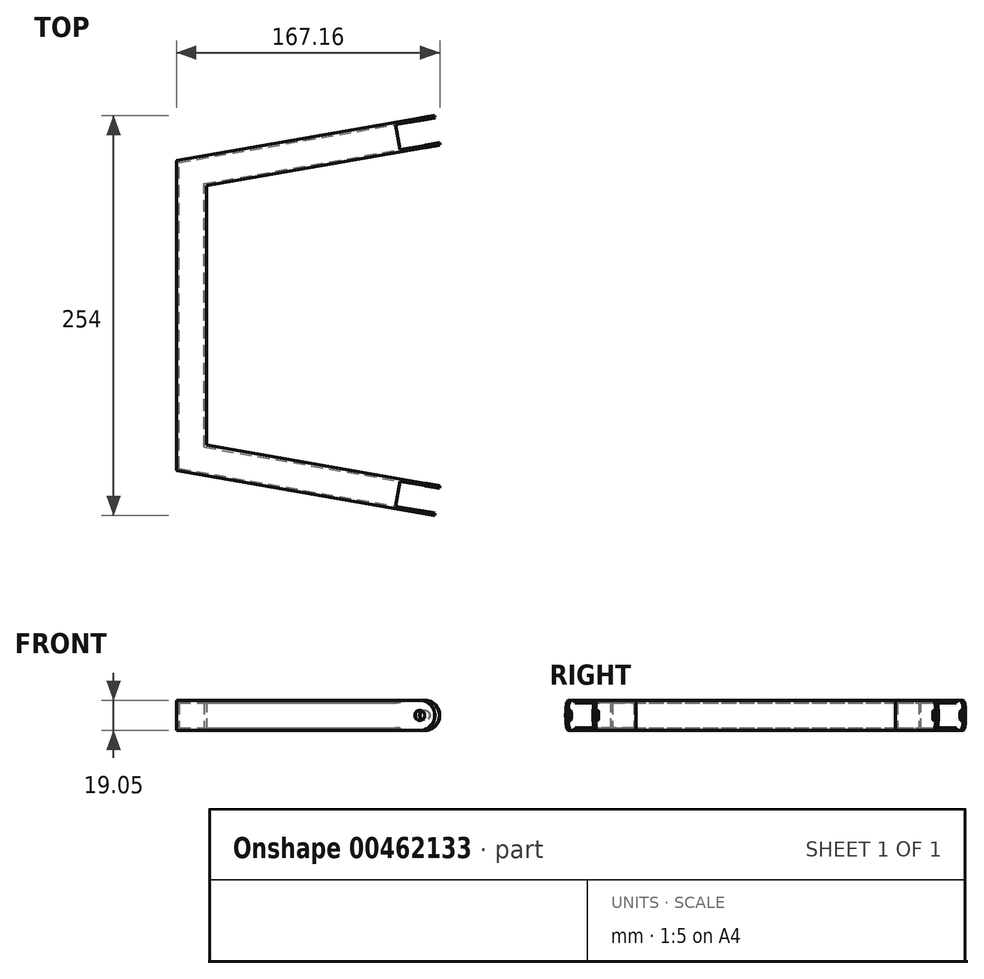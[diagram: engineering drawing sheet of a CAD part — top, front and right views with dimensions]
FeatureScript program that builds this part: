
annotation { "Feature Type Name" : "Feature", "Feature Type Description" : "" }
export const myFeature = defineFeature(function(context is Context, id is Id, definition is map)
    precondition{}
    {
        {
            var Q0;
            Q0=qCreatedBy(makeId("Top.planeOp"),FACE);
            var sketch = newSketch(context, id + "F0", { "sketchPlane" : qUnion([Q0])});
            skLineSegment(sketch, "E0.left", {"start": v(0, 28.57) * mm, "end": v(0, 225.43) * mm});
            skLineSegment(sketch, "E1", {"start": v(0, 127) * mm, "end": v(424.29, 127) * mm, "construction": true});
            skPoint(sketch, "E1.endSnap0", {"position": v(0, 127) * mm});
            skPoint(sketch, "E0.top.start.orphan", {"position": v(0, 254) * mm});
            skPoint(sketch, "E2.orphan", {"position": v(0, 0) * mm});
            skLineSegment(sketch, "E3", {"start": v(0, 225.43) * mm, "end": v(163.89, 254) * mm});
            skLineSegment(sketch, "E4", {"start": v(0, 28.57) * mm, "end": v(163.89, 0) * mm});
            skLineSegment(sketch, "E5.0", {"start": v(19.05, 209.4) * mm, "end": v(167.16, 235.23) * mm});
            skLineSegment(sketch, "E5.1", {"start": v(19.05, 44.6) * mm, "end": v(19.05, 209.4) * mm});
            skLineSegment(sketch, "E5.2", {"start": v(19.05, 44.6) * mm, "end": v(167.16, 18.77) * mm});
            skLineSegment(sketch, "E6", {"start": v(163.89, 254) * mm, "end": v(167.16, 235.23) * mm});
            skLineSegment(sketch, "E7", {"start": v(167.16, 18.77) * mm, "end": v(163.89, 0) * mm});
            skSolve(sketch);
        }
        {
            var Q0;
            Q0 = qSketchRegion(id + "F0", true);
            extrude(context, id + "F1", {"entities" : qUnion([Q0]), "depth" : 19.05 * mm});
        }
        {
            var Q0;
            Q0=makeQuery(id+"F1.opExtrude","SWEPT_FACE",FACE,{"disambiguationData":[OSD([sQuery(id+"F0.wireOp",EDGE,"E7")])]});
            var Q1;
            Q1=makeQuery(id+"F1.opExtrude","SWEPT_FACE",FACE,{"disambiguationData":[OSD([sQuery(id+"F0.wireOp",EDGE,"E6")])]});
            shell(context, id + "F2", {"entities" : qUnion([Q0, Q1]), "thickness" : 1.47 * mm});
        }
        {
            var Q0;
            Q0=makeQuery(id+"F1.opExtrude","SWEPT_FACE",FACE,{"disambiguationData":[OSD([sQuery(id+"F0.wireOp",EDGE,"E7")])]});
            var sketch = newSketch(context, id + "F3", { "sketchPlane" : qUnion([Q0])});
            skLineSegment(sketch, "E8.0", {"start": v(45.73, 19.05) * mm, "end": v(45.73, 0) * mm});
            skLineSegment(sketch, "E8.1", {"start": v(29.62, 19.05) * mm, "end": v(29.62, 0) * mm});
            skLineSegment(sketch, "E9.0", {"start": v(45.73, 19.05) * mm, "end": v(29.62, 19.05) * mm});
            skLineSegment(sketch, "E9.1", {"start": v(45.73, 0) * mm, "end": v(29.62, 0) * mm});
            skPoint(sketch, "E10.orphan", {"position": v(29.62, 17.58) * mm});
            skPoint(sketch, "E11.orphan", {"position": v(45.73, 17.58) * mm});
            skPoint(sketch, "E12.orphan", {"position": v(29.62, 1.47) * mm});
            skPoint(sketch, "E13.orphan", {"position": v(45.73, 1.47) * mm});
            skPoint(sketch, "E14.orphan", {"position": v(47.2, 0) * mm});
            skPoint(sketch, "E15.orphan", {"position": v(28.15, 0) * mm});
            skPoint(sketch, "E16.orphan", {"position": v(28.15, 19.05) * mm});
            skPoint(sketch, "E17.orphan", {"position": v(47.2, 19.05) * mm});
            skSolve(sketch);
        }
        {
            var Q0;
            Q0 = qSketchRegion(id + "F3", true);
            extrude(context, id + "F4", {"entities" : qUnion([Q0]), "operationType" : NewBodyOperationType.REMOVE, "oppositeDirection" : true, "depth" : 25.4 * mm});
        }
        {
            var Q0;
            {var subQ0=sQuery(id+"F0.wireOp",EDGE,"E4");var subQ1=sQuery(id+"F0.wireOp",EDGE,"E7");Q0=makeQuery(id+"F4.boolean.opBoolean","SPLIT",EDGE,{"disambiguationData":[TD([makeQuery(id+"F1.opExtrude","SWEPT_FACE",FACE,{"disambiguationData":[OSD([subQ0])]})])],"derivedFrom":makeQuery(id+"F1.opExtrude","CAP_EDGE",EDGE,{"disambiguationData":[OSD([subQ1])],"isStart":false})});}
            var Q1;
            {var subQ0=sQuery(id+"F0.wireOp",EDGE,"E5.2");var subQ1=sQuery(id+"F0.wireOp",EDGE,"E7");Q1=makeQuery(id+"F4.boolean.opBoolean","SPLIT",EDGE,{"disambiguationData":[TD([makeQuery(id+"F1.opExtrude","SWEPT_FACE",FACE,{"disambiguationData":[OSD([subQ0])]})])],"derivedFrom":makeQuery(id+"F1.opExtrude","CAP_EDGE",EDGE,{"disambiguationData":[OSD([subQ1])],"isStart":false})});}
            var Q2;
            {var subQ0=sQuery(id+"F0.wireOp",EDGE,"E4");var subQ1=sQuery(id+"F0.wireOp",EDGE,"E7");Q2=makeQuery(id+"F4.boolean.opBoolean","SPLIT",EDGE,{"disambiguationData":[TD([makeQuery(id+"F1.opExtrude","SWEPT_FACE",FACE,{"disambiguationData":[OSD([subQ0])]})])],"derivedFrom":makeQuery(id+"F1.opExtrude","CAP_EDGE",EDGE,{"disambiguationData":[OSD([subQ1])],"isStart":true})});}
            var Q3;
            {var subQ0=sQuery(id+"F0.wireOp",EDGE,"E5.2");var subQ1=sQuery(id+"F0.wireOp",EDGE,"E7");Q3=makeQuery(id+"F4.boolean.opBoolean","SPLIT",EDGE,{"disambiguationData":[TD([makeQuery(id+"F1.opExtrude","SWEPT_FACE",FACE,{"disambiguationData":[OSD([subQ0])]})])],"derivedFrom":makeQuery(id+"F1.opExtrude","CAP_EDGE",EDGE,{"disambiguationData":[OSD([subQ1])],"isStart":true})});}
            fillet(context, id + "F5", {"entities" : qUnion([Q0, Q1, Q2, Q3]), "radius" : 9.52 * mm, "tangentPropagation" : true, "allowEdgeOverflow" : false});
        }
        {
            var Q0;
            Q0=makeQuery(id+"F1.opExtrude","SWEPT_FACE",FACE,{"disambiguationData":[OSD([sQuery(id+"F0.wireOp",EDGE,"E4")])]});
            var sketch = newSketch(context, id + "F6", { "sketchPlane" : qUnion([Q0])});
            skCircle(sketch, "E18", {"center": v(151.93, 9.53) * mm, "radius": 3.18 * mm});
            skSolve(sketch);
        }
        {
            var Q0;
            Q0 = qSketchRegion(id + "F6", true);
            extrude(context, id + "F7", {"entities" : qUnion([Q0]), "operationType" : NewBodyOperationType.REMOVE, "endBound" : BoundingType.THROUGH_ALL, "oppositeDirection" : true, "depth" : 25.4 * mm});
        }
        {
            var Q0;
            Q0=makeQuery(id+"F1.opExtrude","SWEPT_FACE",FACE,{"disambiguationData":[OSD([sQuery(id+"F0.wireOp",EDGE,"E6")])]});
            var sketch = newSketch(context, id + "F8", { "sketchPlane" : qUnion([Q0])});
            skLineSegment(sketch, "E19.0", {"start": v(204.5, 19.05) * mm, "end": v(204.5, 0) * mm});
            skLineSegment(sketch, "E20.0", {"start": v(220.6, 19.05) * mm, "end": v(220.6, 0) * mm});
            skLineSegment(sketch, "E21.0", {"start": v(220.6, 0) * mm, "end": v(204.5, 0) * mm});
            skLineSegment(sketch, "E22.0", {"start": v(220.6, 19.05) * mm, "end": v(204.5, 19.05) * mm});
            skPoint(sketch, "E23.orphan", {"position": v(220.6, 1.47) * mm});
            skPoint(sketch, "E24.orphan", {"position": v(204.5, 1.47) * mm});
            skPoint(sketch, "E25.orphan", {"position": v(204.5, 17.58) * mm});
            skPoint(sketch, "E26.orphan", {"position": v(220.6, 17.58) * mm});
            skPoint(sketch, "E27.orphan", {"position": v(203.02, 0) * mm});
            skPoint(sketch, "E28.orphan", {"position": v(222.07, 0) * mm});
            skPoint(sketch, "E29.orphan", {"position": v(222.07, 19.05) * mm});
            skPoint(sketch, "E30.orphan", {"position": v(203.02, 19.05) * mm});
            skSolve(sketch);
        }
        {
            var Q0;
            Q0 = qSketchRegion(id + "F8", true);
            extrude(context, id + "F9", {"entities" : qUnion([Q0]), "operationType" : NewBodyOperationType.REMOVE, "oppositeDirection" : true, "depth" : 25.4 * mm});
        }
        {
            var Q0;
            {var subQ0=sQuery(id+"F0.wireOp",EDGE,"E3");var subQ1=sQuery(id+"F0.wireOp",EDGE,"E6");Q0=makeQuery(id+"F9.boolean.opBoolean","SPLIT",EDGE,{"disambiguationData":[TD([makeQuery(id+"F1.opExtrude","SWEPT_FACE",FACE,{"disambiguationData":[OSD([subQ0])]})])],"derivedFrom":makeQuery(id+"F1.opExtrude","CAP_EDGE",EDGE,{"disambiguationData":[OSD([subQ1])],"isStart":true})});}
            var Q1;
            {var subQ0=sQuery(id+"F0.wireOp",EDGE,"E3");var subQ1=sQuery(id+"F0.wireOp",EDGE,"E6");Q1=makeQuery(id+"F9.boolean.opBoolean","SPLIT",EDGE,{"disambiguationData":[TD([makeQuery(id+"F1.opExtrude","SWEPT_FACE",FACE,{"disambiguationData":[OSD([subQ0])]})])],"derivedFrom":makeQuery(id+"F1.opExtrude","CAP_EDGE",EDGE,{"disambiguationData":[OSD([subQ1])],"isStart":false})});}
            var Q2;
            {var subQ0=sQuery(id+"F0.wireOp",EDGE,"E5.0");var subQ1=sQuery(id+"F0.wireOp",EDGE,"E6");Q2=makeQuery(id+"F9.boolean.opBoolean","SPLIT",EDGE,{"disambiguationData":[TD([makeQuery(id+"F1.opExtrude","SWEPT_FACE",FACE,{"disambiguationData":[OSD([subQ0])]})])],"derivedFrom":makeQuery(id+"F1.opExtrude","CAP_EDGE",EDGE,{"disambiguationData":[OSD([subQ1])],"isStart":false})});}
            var Q3;
            {var subQ0=sQuery(id+"F0.wireOp",EDGE,"E6");var subQ1=sQuery(id+"F0.wireOp",EDGE,"E5.0");Q3=makeQuery(id+"F9.boolean.opBoolean","SPLIT",EDGE,{"disambiguationData":[TD([makeQuery(id+"F1.opExtrude","SWEPT_FACE",FACE,{"disambiguationData":[OSD([subQ1])]})])],"derivedFrom":makeQuery(id+"F1.opExtrude","CAP_EDGE",EDGE,{"disambiguationData":[OSD([subQ0])],"isStart":true})});}
            fillet(context, id + "F10", {"entities" : qUnion([Q0, Q1, Q2, Q3]), "radius" : 9.52 * mm, "tangentPropagation" : true, "allowEdgeOverflow" : false});
        }
        {
            var Q0;
            Q0=makeQuery(id+"F1.opExtrude","SWEPT_FACE",FACE,{"disambiguationData":[OSD([sQuery(id+"F0.wireOp",EDGE,"E3")])]});
            var sketch = newSketch(context, id + "F11", { "sketchPlane" : qUnion([Q0])});
            skCircle(sketch, "E31", {"center": v(-195.56, 9.53) * mm, "radius": 3.18 * mm});
            skSolve(sketch);
        }
        {
            var Q0;
            Q0 = qSketchRegion(id + "F11", true);
            extrude(context, id + "F12", {"entities" : qUnion([Q0]), "operationType" : NewBodyOperationType.REMOVE, "endBound" : BoundingType.THROUGH_ALL, "oppositeDirection" : true, "depth" : 25.4 * mm});
        }
    });
